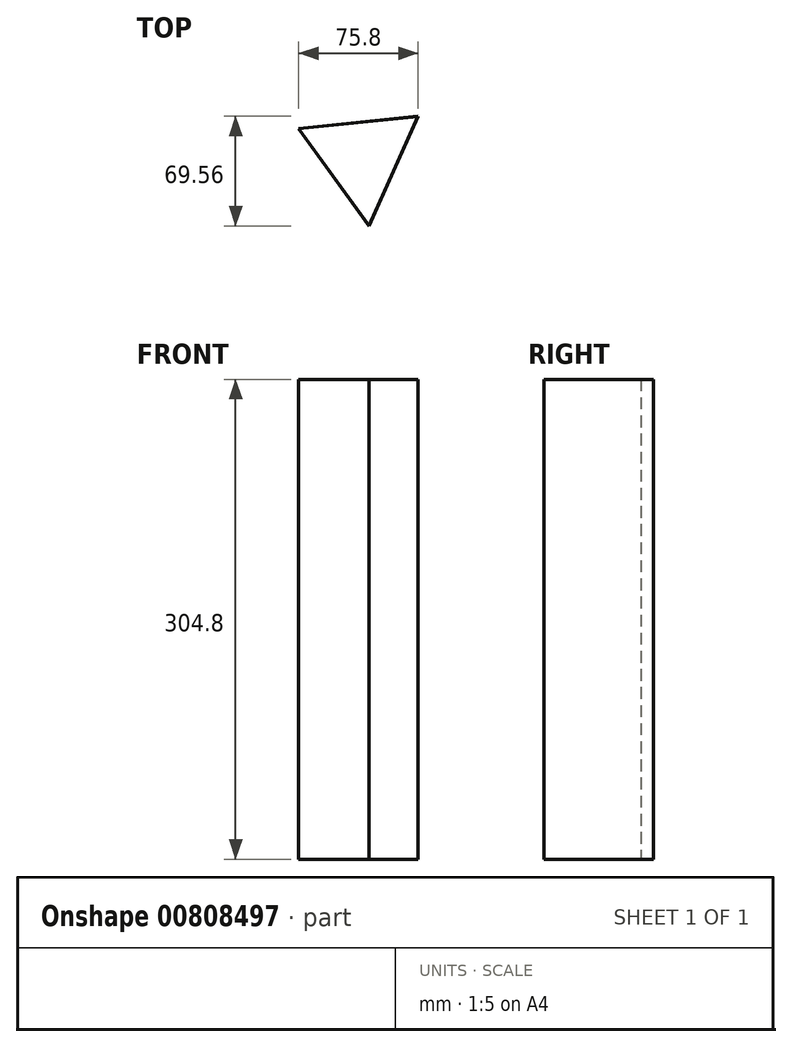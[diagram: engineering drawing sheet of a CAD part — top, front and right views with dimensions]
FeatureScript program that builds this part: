
annotation { "Feature Type Name" : "Feature", "Feature Type Description" : "" }
export const myFeature = defineFeature(function(context is Context, id is Id, definition is map)
    precondition{}
    {
        {
            var Q0;
            Q0=qCreatedBy(makeId("Top.planeOp"),FACE);
            var sketch = newSketch(context, id + "F0", { "sketchPlane" : qUnion([Q0])});
            skCircle(sketch, "E0.cCircle", {"center": v(0, 0) * mm, "radius": 22 * mm, "construction": true});
            skLineSegment(sketch, "E0.0", {"start": v(-40.16, 17.97) * mm, "end": v(35.64, 25.8) * mm});
            skLineSegment(sketch, "E0.1", {"start": v(35.64, 25.8) * mm, "end": v(4.52, -43.76) * mm});
            skLineSegment(sketch, "E0.2", {"start": v(4.52, -43.76) * mm, "end": v(-40.16, 17.97) * mm});
            skPoint(sketch, "E0.0.midPoint", {"position": v(-2.26, 21.88) * mm});
            skSolve(sketch);
        }
        {
            var Q0;
            Q0=makeQuery(id+"F0.imprint","IMPRINT",FACE,{"disambiguationData":[TD([[makeQuery(id+"F0.imprint","IMPRINT",EDGE,{"derivedFrom":sQuery(id+"F0.wireOp",EDGE,"E0.0")}),-1.0]])]});
            extrude(context, id + "F1", {"entities" : qUnion([Q0]), "depth" : 304.8 * mm, "offsetDistance" : 25.4 * mm});
        }
        {
            var Q0;
            Q0=makeQuery(id+"F1.opExtrude","CAP_FACE",FACE,{"disambiguationData":[OSD([sQuery(id+"F0.wireOp",EDGE,"E0.0"),sQuery(id+"F0.wireOp",EDGE,"E0.1"),sQuery(id+"F0.wireOp",EDGE,"E0.2")])],"isStart":false});
            shell(context, id + "F2", {"entities" : qUnion([Q0]), "thickness" : 2 / 127 * mm});
        }
    });
